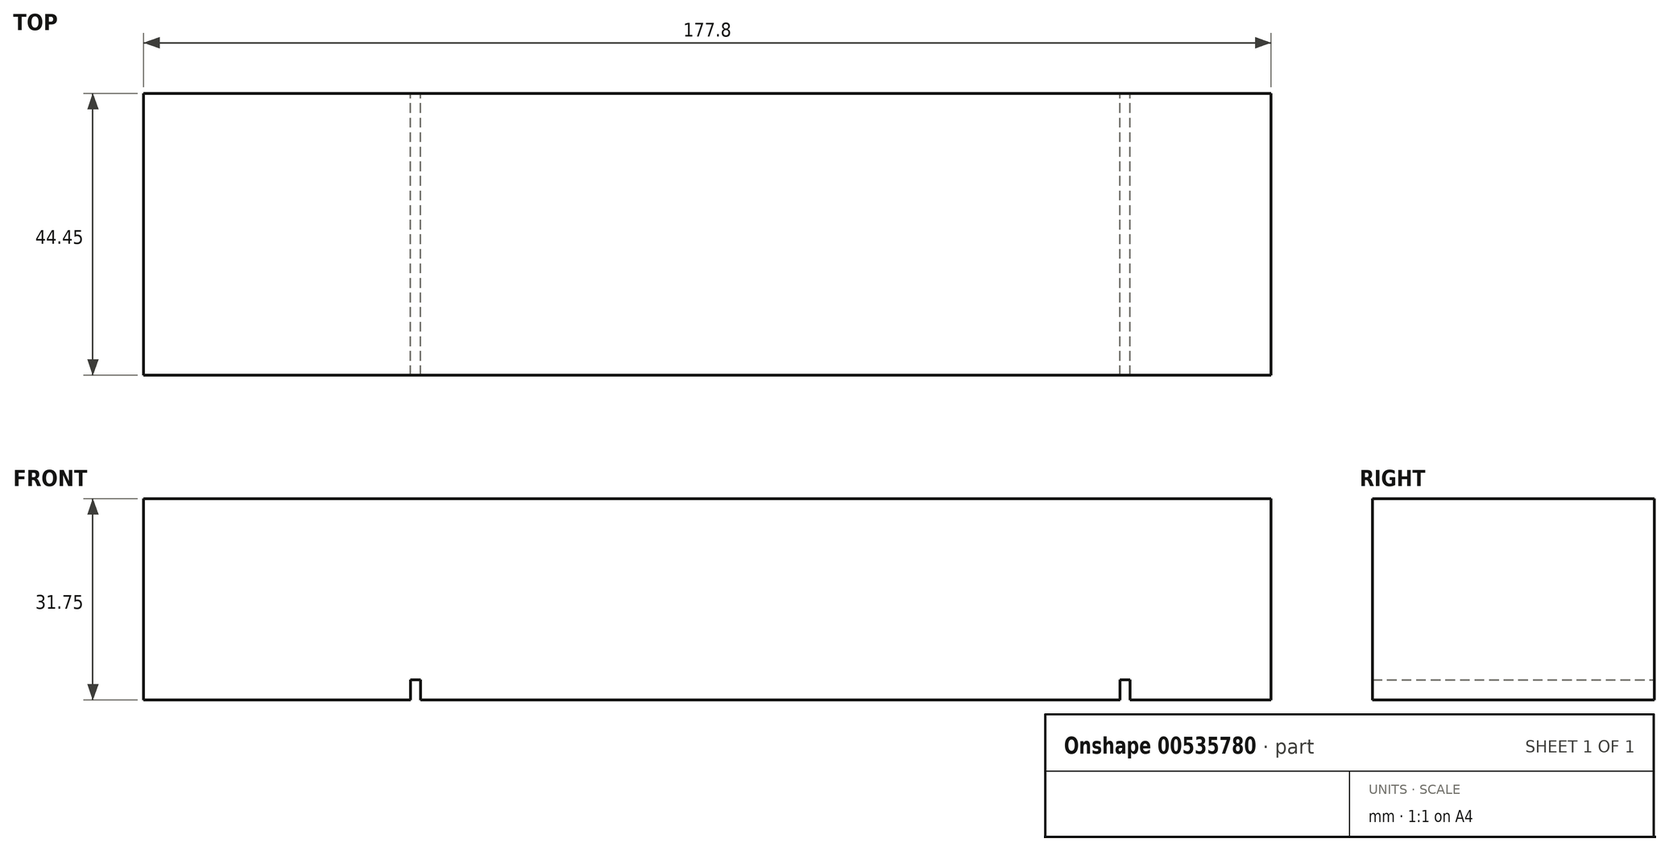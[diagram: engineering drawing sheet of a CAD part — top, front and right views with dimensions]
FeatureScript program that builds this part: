
annotation { "Feature Type Name" : "Feature", "Feature Type Description" : "" }
export const myFeature = defineFeature(function(context is Context, id is Id, definition is map)
    precondition{}
    {
        {
            var Q0;
            Q0=qCreatedBy(makeId("Top.planeOp"),FACE);
            var sketch = newSketch(context, id + "F0", { "sketchPlane" : qUnion([Q0])});
            skLineSegment(sketch, "E0.bottom", {"start": v(0, 0) * mm, "end": v(-177.8, 0) * mm});
            skLineSegment(sketch, "E0.top", {"start": v(0, -44.45) * mm, "end": v(-177.8, -44.45) * mm});
            skLineSegment(sketch, "E0.left", {"start": v(0, 0) * mm, "end": v(0, -44.45) * mm});
            skLineSegment(sketch, "E0.right", {"start": v(-177.8, 0) * mm, "end": v(-177.8, -44.45) * mm});
            skSolve(sketch);
        }
        {
            var Q0;
            Q0=makeQuery(id+"F0.imprint","IMPRINT",FACE,{"disambiguationData":[TD([[makeQuery(id+"F0.imprint","IMPRINT",EDGE,{"derivedFrom":sQuery(id+"F0.wireOp",EDGE,"E0.bottom")}),1.0]])]});
            extrude(context, id + "F1", {"entities" : qUnion([Q0]), "depth" : 31.75 * mm});
        }
        {
            var Q0;
            Q0=makeQuery(id+"F1.opExtrude","CAP_FACE",FACE,{"disambiguationData":[OSD([sQuery(id+"F0.wireOp",EDGE,"E0.bottom"),sQuery(id+"F0.wireOp",EDGE,"E0.top"),sQuery(id+"F0.wireOp",EDGE,"E0.left"),sQuery(id+"F0.wireOp",EDGE,"E0.right")])],"isStart":true});
            var sketch = newSketch(context, id + "F2", { "sketchPlane" : qUnion([Q0])});
            skLineSegment(sketch, "E1.bottom", {"start": v(-135.73, 44.45) * mm, "end": v(-134.14, 44.45) * mm});
            skLineSegment(sketch, "E1.top", {"start": v(-135.73, 0) * mm, "end": v(-134.14, 0) * mm});
            skLineSegment(sketch, "E1.left", {"start": v(-135.73, 44.45) * mm, "end": v(-135.73, 0) * mm});
            skLineSegment(sketch, "E1.right", {"start": v(-134.14, 44.45) * mm, "end": v(-134.14, 0) * mm});
            skLineSegment(sketch, "E2.bottom", {"start": v(-23.81, 44.45) * mm, "end": v(-22.23, 44.45) * mm});
            skLineSegment(sketch, "E2.top", {"start": v(-23.81, 0) * mm, "end": v(-22.23, 0) * mm});
            skLineSegment(sketch, "E2.left", {"start": v(-23.81, 44.45) * mm, "end": v(-23.81, 0) * mm});
            skLineSegment(sketch, "E2.right", {"start": v(-22.23, 44.45) * mm, "end": v(-22.23, 0) * mm});
            skSolve(sketch);
        }
        {
            var Q0;
            Q0=makeQuery(id+"F2.imprint","IMPRINT",FACE,{"disambiguationData":[TD([[makeQuery(id+"F2.imprint","IMPRINT",EDGE,{"derivedFrom":sQuery(id+"F2.wireOp",EDGE,"E2.bottom")}),1.0]])]});
            var Q1;
            Q1=makeQuery(id+"F2.imprint","IMPRINT",FACE,{"disambiguationData":[TD([[makeQuery(id+"F2.imprint","IMPRINT",EDGE,{"derivedFrom":sQuery(id+"F2.wireOp",EDGE,"E1.bottom")}),1.0]])]});
            extrude(context, id + "F3", {"entities" : qUnion([Q0, Q1]), "operationType" : NewBodyOperationType.REMOVE, "oppositeDirection" : true, "depth" : 3.17 * mm});
        }
    });
